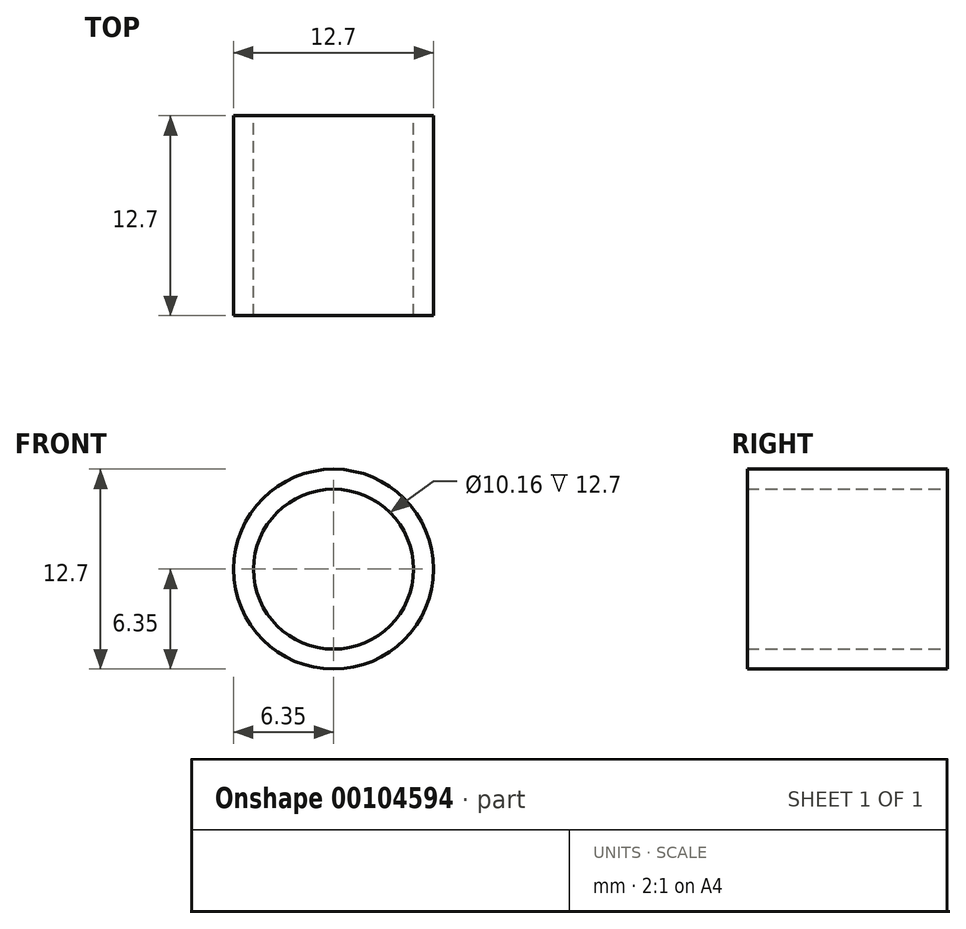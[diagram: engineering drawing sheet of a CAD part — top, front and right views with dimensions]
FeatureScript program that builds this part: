
annotation { "Feature Type Name" : "Feature", "Feature Type Description" : "" }
export const myFeature = defineFeature(function(context is Context, id is Id, definition is map)
    precondition{}
    {
        {
            var Q0;
            Q0=qCreatedBy(makeId("Front.planeOp"),FACE);
            var sketch = newSketch(context, id + "F0", { "sketchPlane" : qUnion([Q0])});
            skCircle(sketch, "E0", {"center": v(0, 0) * mm, "radius": 6.35 * mm});
            skCircle(sketch, "E1", {"center": v(0, 0) * mm, "radius": 5.08 * mm});
            skSolve(sketch);
        }
        {
            var Q0;
            Q0=qCreatedBy(makeId("Right.planeOp"),FACE);
            var sketch = newSketch(context, id + "F1", { "sketchPlane" : qUnion([Q0])});
            skLineSegment(sketch, "E2", {"start": v(0, 0) * mm, "end": v(12.7, 0) * mm});
            skSolve(sketch);
        }
        {
            var Q0;
            Q0=makeQuery(id+"F0.imprint","IMPRINT",FACE,{"disambiguationData":[TD([[makeQuery(id+"F0.imprint","IMPRINT",EDGE,{"derivedFrom":sQuery(id+"F0.wireOp",EDGE,"E0")}),1.0]])]});
            var Q1;
            Q1=sQuery(id+"F1.wireOp",EDGE,"E2");
            sweep(context, id + "F2", {"profiles" : qUnion([Q0]), "path" : qUnion([Q1])});
        }
    });
